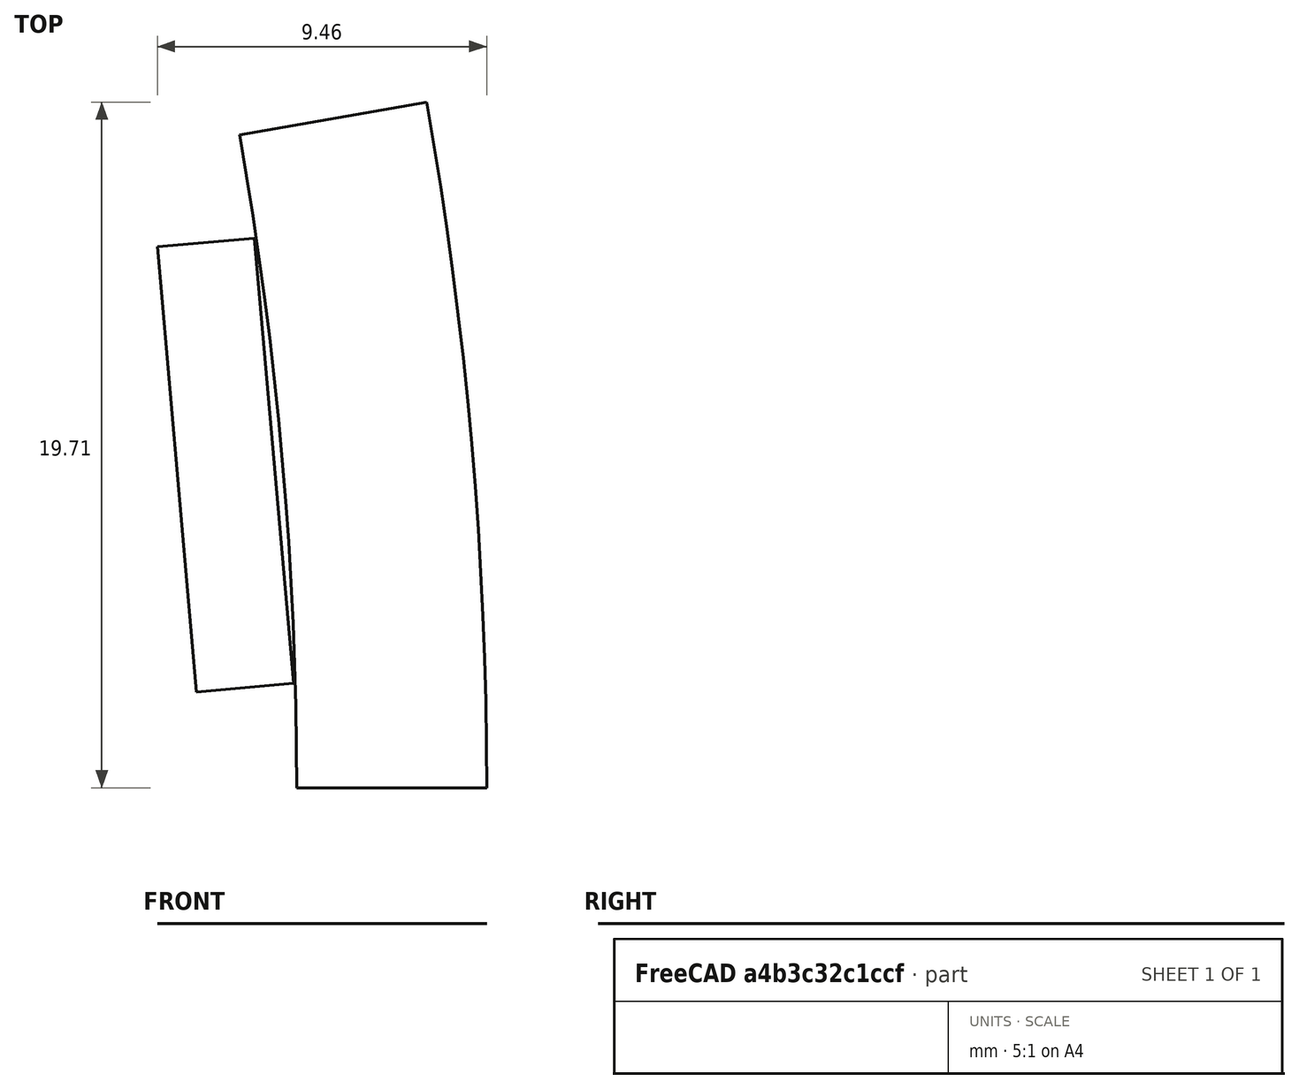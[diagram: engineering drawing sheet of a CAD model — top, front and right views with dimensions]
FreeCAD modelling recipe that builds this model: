
FCSTD DOCUMENT  (FreeCAD 0.18R4 (GitTag))
Label: RotorORBlockMagnetRoundBack
License: All rights reserved
LicenseURL: http://en.wikipedia.org/wiki/All_rights_reserved
objects: Sketcher::SketchObject×5, PartDesign::Body×2, Surface::Filling×2, Spreadsheet::Sheet×1
note: 9 computed .brp shape members not serialized (recipe doc carries the construction recipe); baked Part::Feature solids carry a one-line shape summary decoded from their .brp

FEATURE [Spreadsheet::Sheet] Spreadsheet  label="Variables"
  cells = A2=poleNumber; B2(poleNumber)=36; A3=outerDiameter; B3(outerDiameter)=227; D3=Calc Value; A4=innerDiameter; B4(innerDiameter)=210; D4=Input Value; A5=stackLength; B5(stackLength)=20; A6=stackingFactor; B6(stackingFactor)=0.95; A7=embrace; B7(embrace)=80; A8=contourRatio; B8(contourRatio)=80; A9=magnetAirgap; B9(magnetAirgap)=0.05; A10=poleSeparation; B10(poleSeparation)=2; A11=magnetWidth; B11(magnetWidth)=9; A12=magnetHeight; B12(magnetHeight)=2.8; A13=rib; B13(rib)=0.5; A14=bridgeCurved; B14(bridgeCurved)=0.5; A15=cutTop; B15(cutTop)=0.2; A16=cutBottom; B16(cutBottom)=0.25; A17=segmentAngle; B17(segmentAngle)==360 / poleNumber; A18=movePocketInwards; B18(movePocketInwards)=0.5; A19=cuttingThickness; B19(cuttingThickness)=0.1; A20=magnetLength; B20(magnetLength)==stackLength; A21=cut; B21(cut)=0.2; A22=ribShaft; B22(ribShaft)=0.5; A23=magnetEmbrace; B23(magnetEmbrace)=70; A24=magnetContourRatio; B24(magnetContourRatio)=90; A25=axialMisalignment; B25(axialMisalignment)=0.5
FEATURE [Sketcher::SketchObject] Sketch003  label="RotorSketch"
  MapMode = 5
  Support = -> [XY_Plane]
  expr: Constraints[36] = Variables.innerDiameter / 2 + Variables.magnetHeight + Variables.magnetAirgap
  expr: Constraints[18] = Variables.segmentAngle / 2
  expr: Constraints[0] = Variables.segmentAngle
  expr: Constraints[15] = Variables.outerDiameter / 2
  expr: Constraints[14] = Variables.innerDiameter / 2
  expr: Constraints[29] = Variables.segmentAngle * Variables.magnetEmbrace / 100
  sketch-geometry (18):
    g0: LineSegment [constr] StartX=105 StartY=0 StartZ=0 EndX=113.5 EndY=0 EndZ=0
    g1: LineSegment [constr] StartX=103.405 StartY=18.2331 StartZ=0 EndX=111.776 EndY=19.7091 EndZ=0
    g2: LineSegment [constr] StartX=0 StartY=0 StartZ=0 EndX=105 EndY=0 EndZ=0
    g3: LineSegment [constr] StartX=0 StartY=0 StartZ=0 EndX=103.405 EndY=18.2331 EndZ=0
    g4: ArcOfCircle CenterX=0 CenterY=0 CenterZ=0 NormalX=0 NormalY=0 NormalZ=1 AngleXU=0 Radius=113.5 StartAngle=0 EndAngle=0.174533
    g5: ArcOfCircle [constr] CenterX=0 CenterY=0 CenterZ=0 NormalX=0 NormalY=0 NormalZ=1 AngleXU=0 Radius=105 StartAngle=0 EndAngle=0.174533
    g6: LineSegment [constr] StartX=0 StartY=0 StartZ=0 EndX=113.068 EndY=9.89218 EndZ=0
    g7: LineSegment [constr] StartX=103.8 StartY=18.3027 StartZ=0 EndX=105.401 EndY=0 EndZ=0
    g8: LineSegment [constr] StartX=104.041 StartY=15.549 StartZ=0 EndX=105.16 EndY=2.75372 EndZ=0
    g9: LineSegment [constr] StartX=0 StartY=0 StartZ=0 EndX=104.041 EndY=15.549 EndZ=0
    g10: LineSegment [constr] StartX=0 StartY=0 StartZ=0 EndX=105.16 EndY=2.75372 EndZ=0
    g11: LineSegment [constr] StartX=106.617 StartY=18.7995 StartZ=0 EndX=108.262 EndY=0 EndZ=0
    g12: LineSegment [constr] StartX=0 StartY=0 StartZ=0 EndX=107.44 EndY=9.39975 EndZ=0
    g13: LineSegment [constr] StartX=104.041 StartY=15.549 StartZ=0 EndX=106.88 EndY=15.7974 EndZ=0
    g14: LineSegment [constr] StartX=105.16 StartY=2.75372 StartZ=0 EndX=107.999 EndY=3.00211 EndZ=0
    g15: ArcOfCircle CenterX=0 CenterY=0 CenterZ=0 NormalX=0 NormalY=0 NormalZ=1 AngleXU=0 Radius=108.041 StartAngle=0 EndAngle=0.174533
    g16: LineSegment StartX=106.4 StartY=18.7611 StartZ=0 EndX=111.776 EndY=19.7091 EndZ=0
    g17: LineSegment StartX=108.041 StartY=0 StartZ=0 EndX=113.5 EndY=0 EndZ=0
  constraints (51):
    c: Angle(g0,g1) = 0.174533
    c: Coincident(g2,g-1)
    c: Coincident(g2,g0)
    c: Coincident(g3,g2)
    c: Coincident(g3,g1)
    c: Parallel(g2,g0)
    c: Parallel(g3,g1)
    c: Coincident(g4,g-1)
    c: Coincident(g4,g0)
    c: Coincident(g4,g1)
    c: Coincident(g5,g4)
    c: Coincident(g5,g1)
    c: Coincident(g5,g0)
    c: Angle(g-1,g2) = 0
    c: Radius(g5) = 105
    c: Radius(g4) = 113.5
    c: Coincident(g6,g5)
    c: PointOnObject(g6,g4)
    c: Angle(g-1,g6) = 0.0872665
    c: PointOnObject(g7,g0)
    c: Tangent(g7,g5)
    c: Angle(g6,g7) = 1.5708
    c: PointOnObject(g7,g1)
    c: PointOnObject(g8,g7)
    c: Symmetric(g8,g8,g6)
    c: Coincident(g9,g5)
    c: Coincident(g9,g8)
    c: Coincident(g10,g5)
    c: Coincident(g10,g8)
    c: Angle(g10,g9) = 0.122173
    c: PointOnObject(g11,g1)
    c: PointOnObject(g11,g0)
    c: Angle(g11,g6) = 1.5708
    c: Coincident(g12,g-1)
    c: PointOnObject(g12,g11)
    c: Perpendicular(g12,g11)
    c: Distance(g12) = 107.85
    c: Coincident(g13,g8)
    c: PointOnObject(g13,g11)
    c: Coincident(g14,g8)
    c: PointOnObject(g14,g11)
    c: Angle(g11,g14) = 1.5708
    c: Angle(g13,g11) = 1.5708
    c: Coincident(g15,g4)
    c: PointOnObject(g15,g1)
    c: PointOnObject(g15,g0)
    c: PointOnObject(g13,g15)
    c: Coincident(g16,g15)
    c: Coincident(g16,g4)
    c: Coincident(g17,g15)
    c: Coincident(g17,g4)
FEATURE [Sketcher::SketchObject] Sketch004  label="BoundingBox"
  MapMode = 5
  Support = -> [XY_Plane]
  expr: Constraints[8] = Variables.outerDiameter
  sketch-geometry (6):
    g0: LineSegment StartX=-113.5 StartY=-113.5 StartZ=0 EndX=113.5 EndY=-113.5 EndZ=0
    g1: LineSegment StartX=113.5 StartY=-113.5 StartZ=0 EndX=113.5 EndY=113.5 EndZ=0
    g2: LineSegment StartX=113.5 StartY=113.5 StartZ=0 EndX=-113.5 EndY=113.5 EndZ=0
    g3: LineSegment StartX=-113.5 StartY=113.5 StartZ=0 EndX=-113.5 EndY=-113.5 EndZ=0
    g4: LineSegment [constr] StartX=-113.5 StartY=-113.5 StartZ=0 EndX=113.5 EndY=113.5 EndZ=0
    g5: GeomPoint X=4.4e-15 Y=-1.8e-15 Z=0
  constraints (14):
    c: Coincident(g0,g1)
    c: Coincident(g1,g2)
    c: Coincident(g2,g3)
    c: Coincident(g3,g0)
    c: Horizontal(g0)
    c: Horizontal(g2)
    c: Vertical(g1)
    c: Vertical(g3)
    c: DistanceY(g1,g1) = 227
    c: Equal(g2,g1)
    c: Coincident(g4,g0)
    c: Coincident(g4,g1)
    c: Symmetric(g0,g1,g5)
    c: Coincident(g-1,g5)
FEATURE [Sketcher::SketchObject] Sketch005  label="RotorSideSketch"
  MapMode = 5
  Support = -> [XY_Plane001]
  expr: Constraints[19] = Variables.stackLength / 2 - Variables.axialMisalignment
  expr: Constraints[9] = Variables.outerDiameter / 2
  expr: Constraints[8] = Variables.innerDiameter / 2
  expr: Constraints[7] = Variables.stackLength
  sketch-geometry (8):
    g0: LineSegment StartX=-9.5 StartY=105 StartZ=0 EndX=10.5 EndY=105 EndZ=0
    g1: LineSegment StartX=10.5 StartY=105 StartZ=0 EndX=10.5 EndY=113.5 EndZ=0
    g2: LineSegment StartX=10.5 StartY=113.5 StartZ=0 EndX=-9.5 EndY=113.5 EndZ=0
    g3: LineSegment StartX=-9.5 StartY=113.5 StartZ=0 EndX=-9.5 EndY=105 EndZ=0
    g4: LineSegment StartX=-9.5 StartY=-105 StartZ=0 EndX=10.5 EndY=-105 EndZ=0
    g5: LineSegment StartX=10.5 StartY=-105 StartZ=0 EndX=10.5 EndY=-113.5 EndZ=0
    g6: LineSegment StartX=10.5 StartY=-113.5 StartZ=0 EndX=-9.5 EndY=-113.5 EndZ=0
    g7: LineSegment StartX=-9.5 StartY=-113.5 StartZ=0 EndX=-9.5 EndY=-105 EndZ=0
  constraints (23):
    c: Coincident(g0,g1)
    c: Coincident(g1,g2)
    c: Coincident(g2,g3)
    c: Coincident(g3,g0)
    c: Horizontal(g0)
    c: Vertical(g1)
    c: Vertical(g3)
    c: DistanceX(g2,g2) = 20
    c: DistanceY(g-1,g0) = 105
    c: DistanceY(g-1,g1) = 113.5
    c: Coincident(g4,g5)
    c: Coincident(g5,g6)
    c: Coincident(g6,g7)
    c: Coincident(g7,g4)
    c: Horizontal(g4)
    c: Vertical(g5)
    c: Equal(g4,g0)
    c: Symmetric(g0,g4,g-1)
    c: Horizontal(g2)
    c: DistanceX(g0,g-1) = 9.5
    c: Horizontal(g6)
    c: Vertical(g7)
    c: Equal(g3,g7)
FEATURE [Sketcher::SketchObject] Sketch006  label="MagnetSideSketch"
  MapMode = 5
  Support = -> [XY_Plane001]
  expr: Constraints[21] = Variables.innerDiameter / 2
  expr: Constraints[18] = Variables.stackLength / 2 - Variables.axialMisalignment
  expr: Constraints[17] = Variables.stackLength
  expr: Constraints[5] = Variables.magnetHeight
  sketch-geometry (8):
    g0: LineSegment StartX=-9.5 StartY=105 StartZ=0 EndX=10.5 EndY=105 EndZ=0
    g1: LineSegment StartX=10.5 StartY=105 StartZ=0 EndX=10.5 EndY=107.8 EndZ=0
    g2: LineSegment StartX=-9.5 StartY=107.8 StartZ=0 EndX=-9.5 EndY=105 EndZ=0
    g3: LineSegment StartX=-9.5 StartY=-105 StartZ=0 EndX=10.5 EndY=-105 EndZ=0
    g4: LineSegment StartX=10.5 StartY=-105 StartZ=0 EndX=10.5 EndY=-107.8 EndZ=0
    g5: LineSegment StartX=10.5 StartY=-107.8 StartZ=0 EndX=-9.5 EndY=-107.8 EndZ=0
    g6: LineSegment StartX=-9.5 StartY=-107.8 StartZ=0 EndX=-9.5 EndY=-105 EndZ=0
    g7: LineSegment StartX=-9.5 StartY=107.8 StartZ=0 EndX=10.5 EndY=107.8 EndZ=0
  constraints (22):
    c: Coincident(g0,g1)
    c: Coincident(g2,g0)
    c: Horizontal(g0)
    c: Vertical(g1)
    c: Vertical(g2)
    c: DistanceY(g1,g1) = 2.8
    c: Coincident(g3,g4)
    c: Coincident(g4,g5)
    c: Coincident(g5,g6)
    c: Coincident(g6,g3)
    c: Horizontal(g3)
    c: Vertical(g4)
    c: Vertical(g6)
    c: Equal(g6,g2)
    c: Coincident(g7,g2)
    c: Coincident(g7,g1)
    c: Horizontal(g7)
    c: DistanceX(g5,g5) = 20
    c: DistanceX(g0,g-1) = 9.5
    c: Symmetric(g3,g0,g-1)
    c: Symmetric(g4,g1,g-1)
    c: DistanceY(g-1,g0) = 105
FEATURE [PartDesign::Body] Body001  label="SideView"
  Group = -> [Sketch005,Sketch006]
  Origin = -> Origin001
FEATURE [Sketcher::SketchObject] Sketch  label="MagnetSketch"
  ExternalGeometry = -> [Sketch003]
  MapMode = 5
  Support = -> [XY_Plane]
  expr: Constraints[29] = Variables.segmentAngle / 2
  expr: Constraints[25] = Variables.segmentAngle * Variables.magnetEmbrace / 100
  expr: Constraints[12] = Variables.magnetHeight
  expr: Constraints[11] = Variables.magnetAirgap
  sketch-geometry (11):
    g0: LineSegment StartX=104.041 StartY=15.549 StartZ=0 EndX=106.83 EndY=15.793 EndZ=0
    g1: LineSegment StartX=106.83 StartY=15.793 StartZ=0 EndX=107.95 EndY=2.99775 EndZ=0
    g2: LineSegment StartX=107.95 StartY=2.99775 StartZ=0 EndX=105.16 EndY=2.75372 EndZ=0
    g3: LineSegment StartX=105.16 StartY=2.75372 StartZ=0 EndX=104.041 EndY=15.549 EndZ=0
    g4: LineSegment [constr] StartX=106.83 StartY=15.793 StartZ=0 EndX=106.88 EndY=15.7974 EndZ=0
    g5: LineSegment [constr] StartX=106.83 StartY=15.793 StartZ=0 EndX=106.826 EndY=15.8428 EndZ=0
    g6: LineSegment [constr] StartX=107.95 StartY=2.99775 StartZ=0 EndX=107.954 EndY=2.94794 EndZ=0
    g7: LineSegment [constr] StartX=107.95 StartY=2.99775 StartZ=0 EndX=107.999 EndY=3.00211 EndZ=0
    g8: LineSegment [constr] StartX=0 StartY=0 StartZ=0 EndX=105.16 EndY=2.75372 EndZ=0
    g9: LineSegment [constr] StartX=0 StartY=0 StartZ=0 EndX=104.041 EndY=15.549 EndZ=0
    g10: LineSegment [constr] StartX=0 StartY=0 StartZ=0 EndX=104.6 EndY=9.15135 EndZ=0
  constraints (30):
    c: Coincident(g1,g0)
    c: Coincident(g2,g1)
    c: Coincident(g3,g2)
    c: Coincident(g3,g0)
    c: Angle(g1,g2) = 1.5708
    c: Equal(g0,g2)
    c: Coincident(g4,g0)
    c: Coincident(g5,g0)
    c: Angle(g4,g5) = 1.5708
    c: Equal(g4,g5)
    c: Angle(g1,g4) = 1.5708
    c: Distance(g4) = 0.05
    c: Distance(g2) = 2.8
    c: Coincident(g6,g1)
    c: Angle(g2,g6) = 1.5708
    c: Equal(g6,g5)
    c: PointOnObject(g4,g-3)
    c: Coincident(g7,g1)
    c: Angle(g6,g7) = 1.5708
    c: Equal(g4,g7)
    c: PointOnObject(g7,g-3)
    c: Coincident(g8,g-1)
    c: Coincident(g8,g2)
    c: Coincident(g9,g-1)
    c: Coincident(g9,g0)
    c: Angle(g8,g9) = 0.122173
    c: Coincident(g10,g-1)
    c: Symmetric(g0,g2,g10)
    c: PointOnObject(g10,g3)
    c: Angle(g-1,g10) = 0.0872665
FEATURE [PartDesign::Body] Body  label="TopView"
  Group = -> [Sketch003,Sketch004,Sketch]
  Origin = -> Origin
FEATURE [Surface::Filling] Surface  label="Magnet_Surface"
  Anisotropy = false
  BoundaryEdges = -> [Sketch]
  BoundaryOrder = [0,0,0,0]
  Degree = 3
  Iterations = 2
  MaximumDegree = 8
  MaximumSegments = 9
  PointsOnCurve = 15
  TolAngular = 0.01
  TolCurvature = 0.1
  Tolerance2d = 1e-05
  Tolerance3d = 0.0001
FEATURE [Surface::Filling] Surface001  label="Rotor_Surface"
  Anisotropy = false
  BoundaryEdges = -> [Sketch003]
  BoundaryOrder = [0,0,0,0]
  Degree = 3
  Iterations = 2
  MaximumDegree = 8
  MaximumSegments = 9
  PointsOnCurve = 15
  TolAngular = 0.01
  TolCurvature = 0.1
  Tolerance2d = 1e-05
  Tolerance3d = 0.0001
